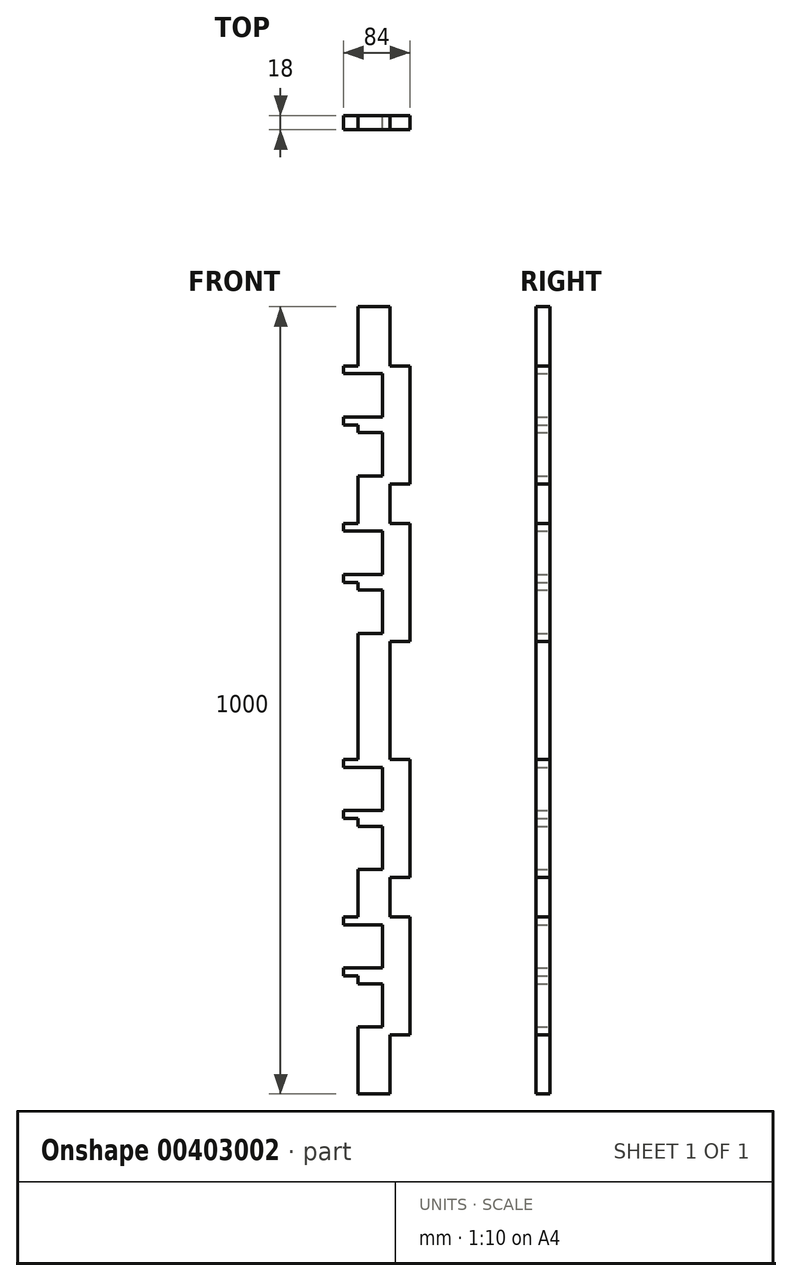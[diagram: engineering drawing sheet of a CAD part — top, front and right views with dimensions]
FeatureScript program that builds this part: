
annotation { "Feature Type Name" : "Feature", "Feature Type Description" : "" }
export const myFeature = defineFeature(function(context is Context, id is Id, definition is map)
    precondition{}
    {
        {
            var Q0;
            Q0=qCreatedBy(makeId("Front.planeOp"),FACE);
            var sketch = newSketch(context, id + "F0", { "sketchPlane" : qUnion([Q0])});
            skLineSegment(sketch, "E0.right", {"start": v(41, 0) * mm, "end": v(41, 75) * mm});
            skLineSegment(sketch, "E1.bottom", {"start": v(41, 925) * mm, "end": v(66, 925) * mm});
            skLineSegment(sketch, "E1.top", {"start": v(41, 775) * mm, "end": v(66, 775) * mm});
            skLineSegment(sketch, "E1.right", {"start": v(66, 925) * mm, "end": v(66, 775) * mm});
            skLineSegment(sketch, "E2.bottom", {"start": v(41, 425) * mm, "end": v(66, 425) * mm});
            skLineSegment(sketch, "E2.top", {"start": v(41, 275) * mm, "end": v(66, 275) * mm});
            skLineSegment(sketch, "E2.right", {"start": v(66, 425) * mm, "end": v(66, 275) * mm});
            skLineSegment(sketch, "E3.trimOffspring", {"start": v(41, 925) * mm, "end": v(41, 1000) * mm});
            skLineSegment(sketch, "E4.trimOffspring", {"start": v(41, 425) * mm, "end": v(41, 575) * mm});
            skLineSegment(sketch, "E5.bottom", {"start": v(66, 725) * mm, "end": v(41, 725) * mm});
            skLineSegment(sketch, "E5.top", {"start": v(66, 575) * mm, "end": v(41, 575) * mm});
            skLineSegment(sketch, "E5.right", {"start": v(66, 725) * mm, "end": v(66, 575) * mm});
            skLineSegment(sketch, "E6.bottom", {"start": v(66, 225) * mm, "end": v(41, 225) * mm});
            skLineSegment(sketch, "E6.top", {"start": v(66, 75) * mm, "end": v(41, 75) * mm});
            skLineSegment(sketch, "E6.right", {"start": v(66, 225) * mm, "end": v(66, 75) * mm});
            skLineSegment(sketch, "E7.trimOffspring", {"start": v(41, 725) * mm, "end": v(41, 775) * mm});
            skLineSegment(sketch, "E8.trimOffspring", {"start": v(41, 225) * mm, "end": v(41, 275) * mm});
            skPoint(sketch, "E9.orphan", {"position": v(0, 0) * mm});
            skLineSegment(sketch, "E10.bottom", {"start": v(-18, 925) * mm, "end": v(0, 925) * mm});
            skLineSegment(sketch, "E10.left", {"start": v(0, 1000) * mm, "end": v(0, 925) * mm});
            skLineSegment(sketch, "E10.right", {"start": v(-18, 925) * mm, "end": v(-18, 915) * mm});
            skLineSegment(sketch, "E11.bottom", {"start": v(-18, 725) * mm, "end": v(0, 725) * mm});
            skLineSegment(sketch, "E11.right", {"start": v(-18, 725) * mm, "end": v(-18, 715) * mm});
            skLineSegment(sketch, "E12.bottom", {"start": v(-18, 425) * mm, "end": v(0, 425) * mm});
            skLineSegment(sketch, "E12.right", {"start": v(-18, 425) * mm, "end": v(-18, 415) * mm});
            skLineSegment(sketch, "E13.bottom", {"start": v(-18, 225) * mm, "end": v(0, 225) * mm});
            skLineSegment(sketch, "E14.bottom", {"start": v(-18, 850) * mm, "end": v(0, 850) * mm});
            skLineSegment(sketch, "E14.top", {"start": v(-18, 650) * mm, "end": v(0, 650) * mm});
            skLineSegment(sketch, "E15.bottom", {"start": v(-18, 350) * mm, "end": v(0, 350) * mm});
            skLineSegment(sketch, "E15.top", {"start": v(-18, 150) * mm, "end": v(0, 150) * mm});
            skLineSegment(sketch, "E16", {"start": v(0, 850) * mm, "end": v(0, 840) * mm});
            skLineSegment(sketch, "E17", {"start": v(0, 650) * mm, "end": v(0, 640) * mm});
            skLineSegment(sketch, "E18", {"start": v(0, 350) * mm, "end": v(0, 340) * mm});
            skLineSegment(sketch, "E19", {"start": v(0, 150) * mm, "end": v(0, 140) * mm});
            skLineSegment(sketch, "E20", {"start": v(0, 1000) * mm, "end": v(41, 1000) * mm});
            skLineSegment(sketch, "E21", {"start": v(0, 0) * mm, "end": v(41, 0) * mm});
            skLineSegment(sketch, "E22", {"start": v(-18, 150) * mm, "end": v(-18, 160) * mm});
            skLineSegment(sketch, "E23.bottom", {"start": v(-18, 915) * mm, "end": v(31, 915) * mm});
            skLineSegment(sketch, "E23.top", {"start": v(-18, 860) * mm, "end": v(31, 860) * mm});
            skLineSegment(sketch, "E23.right", {"start": v(31, 915) * mm, "end": v(31, 860) * mm});
            skLineSegment(sketch, "E24.bottom", {"start": v(-18, 715) * mm, "end": v(31, 715) * mm});
            skLineSegment(sketch, "E24.top", {"start": v(-18, 660) * mm, "end": v(31, 660) * mm});
            skLineSegment(sketch, "E24.right", {"start": v(31, 715) * mm, "end": v(31, 660) * mm});
            skLineSegment(sketch, "E25.bottom", {"start": v(-18, 415) * mm, "end": v(31, 415) * mm});
            skLineSegment(sketch, "E25.top", {"start": v(-18, 360) * mm, "end": v(31, 360) * mm});
            skLineSegment(sketch, "E25.right", {"start": v(31, 415) * mm, "end": v(31, 360) * mm});
            skLineSegment(sketch, "E26.bottom", {"start": v(-18, 215) * mm, "end": v(31, 215) * mm});
            skLineSegment(sketch, "E26.top", {"start": v(-18, 160) * mm, "end": v(31, 160) * mm});
            skLineSegment(sketch, "E26.right", {"start": v(31, 215) * mm, "end": v(31, 160) * mm});
            skLineSegment(sketch, "E27.trimOffspring", {"start": v(-18, 860) * mm, "end": v(-18, 850) * mm});
            skLineSegment(sketch, "E28.trimOffspring", {"start": v(-18, 660) * mm, "end": v(-18, 650) * mm});
            skLineSegment(sketch, "E29.trimOffspring", {"start": v(-18, 360) * mm, "end": v(-18, 350) * mm});
            skLineSegment(sketch, "E30.trimOffspring", {"start": v(-18, 215) * mm, "end": v(-18, 225) * mm});
            skLineSegment(sketch, "E31.bottom", {"start": v(0, 840) * mm, "end": v(31, 840) * mm});
            skLineSegment(sketch, "E31.top", {"start": v(0, 785) * mm, "end": v(31, 785) * mm});
            skLineSegment(sketch, "E31.right", {"start": v(31, 840) * mm, "end": v(31, 785) * mm});
            skLineSegment(sketch, "E32.bottom", {"start": v(0, 640) * mm, "end": v(31, 640) * mm});
            skLineSegment(sketch, "E32.top", {"start": v(0, 585) * mm, "end": v(31, 585) * mm});
            skLineSegment(sketch, "E32.right", {"start": v(31, 640) * mm, "end": v(31, 585) * mm});
            skLineSegment(sketch, "E33.bottom", {"start": v(0, 340) * mm, "end": v(31, 340) * mm});
            skLineSegment(sketch, "E33.top", {"start": v(0, 285) * mm, "end": v(31, 285) * mm});
            skLineSegment(sketch, "E33.right", {"start": v(31, 340) * mm, "end": v(31, 285) * mm});
            skLineSegment(sketch, "E34.bottom", {"start": v(0, 140) * mm, "end": v(31, 140) * mm});
            skLineSegment(sketch, "E34.top", {"start": v(0, 85) * mm, "end": v(31, 85) * mm});
            skLineSegment(sketch, "E34.right", {"start": v(31, 140) * mm, "end": v(31, 85) * mm});
            skLineSegment(sketch, "E35.trimOffspring", {"start": v(0, 785) * mm, "end": v(0, 725) * mm});
            skLineSegment(sketch, "E36.trimOffspring", {"start": v(0, 585) * mm, "end": v(0, 425) * mm});
            skLineSegment(sketch, "E37.trimOffspring", {"start": v(0, 285) * mm, "end": v(0, 225) * mm});
            skLineSegment(sketch, "E38.trimOffspring", {"start": v(0, 85) * mm, "end": v(0, 0) * mm});
            skSolve(sketch);
        }
        {
            var Q0;
            Q0=makeQuery(id+"F0.imprint","IMPRINT",FACE,{"disambiguationData":[TD([[makeQuery(id+"F0.imprint","IMPRINT",EDGE,{"derivedFrom":sQuery(id+"F0.wireOp",EDGE,"E0.right")}),1.0]])]});
            extrude(context, id + "F1", {"entities" : qUnion([Q0]), "depth" : 18 * mm});
        }
    });
